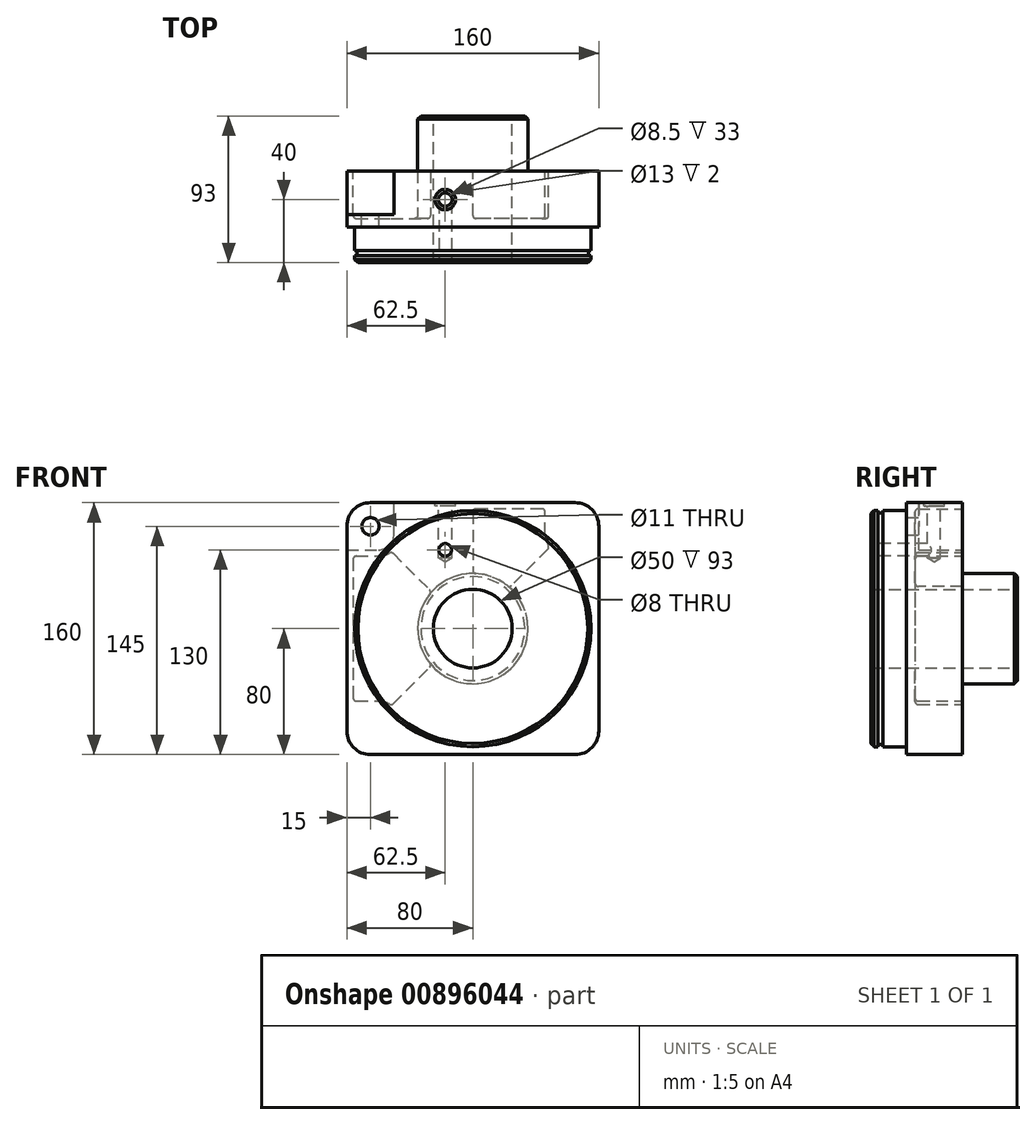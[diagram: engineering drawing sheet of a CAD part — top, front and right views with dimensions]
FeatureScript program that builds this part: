
annotation { "Feature Type Name" : "Feature", "Feature Type Description" : "" }
export const myFeature = defineFeature(function(context is Context, id is Id, definition is map)
    precondition{}
    {
        {
            var Q0;
            Q0=qCreatedBy(makeId("Front.planeOp"),FACE);
            var sketch = newSketch(context, id + "F0", { "sketchPlane" : qUnion([Q0])});
            skLineSegment(sketch, "E0.bottom", {"start": v(65, -80) * mm, "end": v(-65, -80) * mm});
            skLineSegment(sketch, "E0.top", {"start": v(65, 80) * mm, "end": v(-65, 80) * mm});
            skLineSegment(sketch, "E0.left", {"start": v(80, -65) * mm, "end": v(80, 65) * mm});
            skLineSegment(sketch, "E0.right", {"start": v(-80, -65) * mm, "end": v(-80, 65) * mm});
            skPoint(sketch, "E0.middle", {"position": v(0, 0) * mm});
            skPoint(sketch, "E1.visualSharp", {"position": v(-80, 80) * mm});
            skArc(sketch, "E1.filletArc", {"start": v(-65, 80) * mm, "mid": v(-75.6, 75.6) * mm, "end": v(-80, 65) * mm});
            skPoint(sketch, "E2.visualSharp", {"position": v(80, 80) * mm});
            skArc(sketch, "E2.filletArc", {"start": v(80, 65) * mm, "mid": v(75.6, 75.6) * mm, "end": v(65, 80) * mm});
            skPoint(sketch, "E3.visualSharp", {"position": v(80, -80) * mm});
            skArc(sketch, "E3.filletArc", {"start": v(65, -80) * mm, "mid": v(75.6, -75.6) * mm, "end": v(80, -65) * mm});
            skPoint(sketch, "E4.visualSharp", {"position": v(-80, -80) * mm});
            skArc(sketch, "E4.filletArc", {"start": v(-80, -65) * mm, "mid": v(-75.6, -75.6) * mm, "end": v(-65, -80) * mm});
            skLineSegment(sketch, "E5", {"start": v(-80, 50) * mm, "end": v(-60, 50) * mm});
            skLineSegment(sketch, "E6", {"start": v(-50, 60) * mm, "end": v(-50, 80) * mm});
            skPoint(sketch, "E7.visualSharp", {"position": v(-50, 50) * mm});
            skArc(sketch, "E7.filletArc", {"start": v(-60, 50) * mm, "mid": v(-52.93, 52.93) * mm, "end": v(-50, 60) * mm});
            skCircle(sketch, "E8", {"center": v(-65, 65) * mm, "radius": 5.5 * mm});
            skLineSegment(sketch, "E9", {"start": v(0, 0) * mm, "end": v(-65, 65) * mm, "construction": true});
            skLineSegment(sketch, "E10.0", {"start": v(-46, 60) * mm, "end": v(-46, 74) * mm, "construction": true});
            skArc(sketch, "E10.1", {"start": v(-60, 46) * mm, "mid": v(-56.31, 46.5) * mm, "end": v(-52.89, 47.94) * mm});
            skLineSegment(sketch, "E10.2", {"start": v(-74, 46) * mm, "end": v(-60, 46) * mm});
            skCircle(sketch, "E11", {"center": v(0, 0) * mm, "radius": 35 * mm});
            skLineSegment(sketch, "E12", {"start": v(-76, 44) * mm, "end": v(-76, 0) * mm});
            skLineSegment(sketch, "E13", {"start": v(-50.46, 47.63) * mm, "end": v(-26.12, 23.3) * mm});
            skLineSegment(sketch, "E14", {"start": v(-47.63, 50.46) * mm, "end": v(-23.3, 26.12) * mm, "construction": true});
            skLineSegment(sketch, "E15", {"start": v(-44, 76) * mm, "end": v(-2, 76) * mm, "construction": true});
            skLineSegment(sketch, "E16", {"start": v(0, 74) * mm, "end": v(0, 35) * mm});
            skArc(sketch, "E17.trimOffspring", {"start": v(-47.94, 52.89) * mm, "mid": v(-46.5, 56.31) * mm, "end": v(-46, 60) * mm, "construction": true});
            skLineSegment(sketch, "E18.MirrorCS", {"start": v(-76, -44) * mm, "end": v(-76, 0) * mm});
            skLineSegment(sketch, "E19.MirrorCS", {"start": v(-74, -46) * mm, "end": v(-60, -46) * mm});
            skArc(sketch, "E20.MirrorCS", {"start": v(-60, -46) * mm, "mid": v(-56.31, -46.5) * mm, "end": v(-52.89, -47.94) * mm});
            skLineSegment(sketch, "E21.MirrorCS", {"start": v(-50.46, -47.63) * mm, "end": v(-26.12, -23.3) * mm});
            skPoint(sketch, "E22.visualSharp", {"position": v(0, 76) * mm});
            skArc(sketch, "E22.filletArc", {"start": v(0, 74) * mm, "mid": v(-0.59, 75.41) * mm, "end": v(-2, 76) * mm, "construction": true});
            skPoint(sketch, "E23.visualSharp", {"position": v(-46, 76) * mm});
            skArc(sketch, "E23.filletArc", {"start": v(-44, 76) * mm, "mid": v(-45.41, 75.41) * mm, "end": v(-46, 74) * mm, "construction": true});
            skPoint(sketch, "E24.visualSharp", {"position": v(-48.79, 51.62) * mm});
            skArc(sketch, "E24.filletArc", {"start": v(-47.94, 52.89) * mm, "mid": v(-48.2, 51.62) * mm, "end": v(-47.63, 50.46) * mm, "construction": true});
            skPoint(sketch, "E25.visualSharp", {"position": v(-51.62, 48.79) * mm});
            skArc(sketch, "E25.filletArc", {"start": v(-50.46, 47.63) * mm, "mid": v(-51.62, 48.2) * mm, "end": v(-52.89, 47.94) * mm});
            skPoint(sketch, "E26.visualSharp", {"position": v(-76, 46) * mm});
            skArc(sketch, "E26.filletArc", {"start": v(-74, 46) * mm, "mid": v(-75.41, 45.41) * mm, "end": v(-76, 44) * mm});
            skPoint(sketch, "E27.visualSharp", {"position": v(-76, -46) * mm});
            skArc(sketch, "E27.filletArc", {"start": v(-76, -44) * mm, "mid": v(-75.41, -45.41) * mm, "end": v(-74, -46) * mm});
            skPoint(sketch, "E28.visualSharp", {"position": v(-51.62, -48.79) * mm});
            skArc(sketch, "E28.filletArc", {"start": v(-52.89, -47.94) * mm, "mid": v(-51.62, -48.2) * mm, "end": v(-50.46, -47.63) * mm});
            skLineSegment(sketch, "E29.MirrorCS", {"start": v(44, 76) * mm, "end": v(2, 76) * mm});
            skArc(sketch, "E30.MirrorCS", {"start": v(0, 74) * mm, "mid": v(0.59, 75.41) * mm, "end": v(2, 76) * mm});
            skArc(sketch, "E31.MirrorCS", {"start": v(44, 76) * mm, "mid": v(45.41, 75.41) * mm, "end": v(46, 74) * mm});
            skLineSegment(sketch, "E32.MirrorCS", {"start": v(46, 60) * mm, "end": v(46, 74) * mm});
            skArc(sketch, "E33.MirrorCS", {"start": v(47.94, 52.89) * mm, "mid": v(46.5, 56.31) * mm, "end": v(46, 60) * mm});
            skArc(sketch, "E34.MirrorCS", {"start": v(47.94, 52.89) * mm, "mid": v(48.2, 51.62) * mm, "end": v(47.63, 50.46) * mm});
            skLineSegment(sketch, "E35.MirrorCS", {"start": v(47.63, 50.46) * mm, "end": v(23.3, 26.12) * mm});
            skSolve(sketch);
        }
        {
            var Q0;
            Q0 = qSketchRegion(id + "F0", true);
            var Q1;
            Q1=makeQuery(id+"F0.imprint","IMPRINT",FACE,{"disambiguationData":[TD([[makeQuery(id+"F0.imprint","IMPRINT",EDGE,{"derivedFrom":sQuery(id+"F0.wireOp",EDGE,"E10.0")}),-1.0]])]});
            var Q2;
            {var subQ0=sQuery(id+"F0.wireOp",EDGE,"E11");var subQ1=makeQuery(id+"F0.imprint","INTERSECT",VERTEX,{"derivedFrom":[subQ0,sQuery(id+"F0.wireOp",EDGE,"E14")]});Q2=makeQuery(id+"F0.imprint","IMPRINT",FACE,{"disambiguationData":[TD([[makeQuery(id+"F0.imprint","IMPRINT",EDGE,{"disambiguationData":[TD([[subQ1,1.0]])],"derivedFrom":subQ0}),1.0]])]});}
            var Q3;
            Q3=makeQuery(id+"F0.imprint","IMPRINT",FACE,{"disambiguationData":[TD([[makeQuery(id+"F0.imprint","IMPRINT",EDGE,{"derivedFrom":sQuery(id+"F0.wireOp",EDGE,"E10.1")}),-1.0]])]});
            var Q4;
            Q4=makeQuery(id+"F0.imprint","IMPRINT",FACE,{"disambiguationData":[TD([[makeQuery(id+"F0.imprint","IMPRINT",EDGE,{"derivedFrom":sQuery(id+"F0.wireOp",EDGE,"E8")}),1.0]])]});
            var Q5;
            {var subQ0=sQuery(id+"F0.wireOp",EDGE,"E16");Q5=makeQuery(id+"F0.imprint","IMPRINT",FACE,{"disambiguationData":[TD([[makeQuery(id+"F0.imprint","IMPRINT",EDGE,{"derivedFrom":subQ0}),1.0]])]});}
            extrude(context, id + "F1", {"entities" : qUnion([Q0, Q1, Q2, Q3, Q4, Q5]), "depth" : (58 - 22.5) * mm, "offsetDistance" : 25 * mm});
        }
        {
            var Q0;
            {var subQ0=sQuery(id+"F0.wireOp",EDGE,"E11");var subQ1=makeQuery(id+"F0.imprint","INTERSECT",VERTEX,{"derivedFrom":[subQ0,sQuery(id+"F0.wireOp",EDGE,"E14")]});Q0=makeQuery(id+"F0.imprint","IMPRINT",FACE,{"disambiguationData":[TD([[makeQuery(id+"F0.imprint","IMPRINT",EDGE,{"disambiguationData":[TD([[subQ1,1.0]])],"derivedFrom":subQ0}),1.0]])]});}
            extrude(context, id + "F2", {"entities" : qUnion([Q0]), "operationType" : NewBodyOperationType.ADD, "oppositeDirection" : true, "depth" : (93 - 58) * mm, "offsetDistance" : 25 * mm});
        }
        {
            var Q0;
            Q0=makeQuery(id+"F0.imprint","IMPRINT",FACE,{"disambiguationData":[TD([[makeQuery(id+"F0.imprint","IMPRINT",EDGE,{"derivedFrom":sQuery(id+"F0.wireOp",EDGE,"E8")}),1.0]])]});
            var Q1;
            Q1=makeQuery(id+"F1.opExtrude","CAP_FACE",FACE,{"disambiguationData":[OSD([sQuery(id+"F0.wireOp",EDGE,"E0.bottom"),sQuery(id+"F0.wireOp",EDGE,"E0.top"),sQuery(id+"F0.wireOp",EDGE,"E0.left"),sQuery(id+"F0.wireOp",EDGE,"E0.right"),sQuery(id+"F0.wireOp",EDGE,"E1.filletArc"),sQuery(id+"F0.wireOp",EDGE,"E2.filletArc"),sQuery(id+"F0.wireOp",EDGE,"E3.filletArc"),sQuery(id+"F0.wireOp",EDGE,"E4.filletArc")])],"isStart":false});
            extrude(context, id + "F3", {"entities" : qUnion([Q0]), "operationType" : NewBodyOperationType.REMOVE, "endBound" : BoundingType.UP_TO_SURFACE, "depth" : 25 * mm, "endBoundEntityFace" : qUnion([Q1]), "offsetDistance" : 25 * mm});
        }
        {
            var Q0;
            {var subQ0=sQuery(id+"F0.wireOp",EDGE,"E1.filletArc");Q0=makeQuery(id+"F0.imprint","IMPRINT",FACE,{"disambiguationData":[TD([[makeQuery(id+"F0.imprint","IMPRINT",EDGE,{"derivedFrom":subQ0}),1.0]])]});}
            extrude(context, id + "F4", {"entities" : qUnion([Q0]), "operationType" : NewBodyOperationType.REMOVE, "depth" : (35.5 - 8) * mm, "offsetDistance" : 25 * mm});
        }
        {
            var Q0;
            {var subQ0=sQuery(id+"F0.wireOp",EDGE,"E16");Q0=makeQuery(id+"F0.imprint","IMPRINT",FACE,{"disambiguationData":[TD([[makeQuery(id+"F0.imprint","IMPRINT",EDGE,{"derivedFrom":subQ0}),1.0]])]});}
            extrude(context, id + "F5", {"entities" : qUnion([Q0]), "operationType" : NewBodyOperationType.REMOVE, "depth" : 30 * mm, "offsetDistance" : 25 * mm});
        }
        {
            var Q0;
            Q0=makeQuery(id+"F0.imprint","IMPRINT",FACE,{"disambiguationData":[TD([[makeQuery(id+"F0.imprint","IMPRINT",EDGE,{"derivedFrom":sQuery(id+"F0.wireOp",EDGE,"E10.1")}),-1.0]])]});
            extrude(context, id + "F6", {"entities" : qUnion([Q0]), "operationType" : NewBodyOperationType.REMOVE, "depth" : 30 * mm, "offsetDistance" : 25 * mm});
        }
        {
            var Q0;
            Q0=makeQuery(id+"F5.boolean.opBoolean","COPY",EDGE,{"derivedFrom":makeQuery(id+"F5.opExtrude","SWEPT_EDGE",EDGE,{"disambiguationData":[OSD([sQuery(id+"F0.wireOp",EDGE,"E11"),sQuery(id+"F0.wireOp",EDGE,"E16")])]})});
            var Q1;
            Q1=makeQuery(id+"F5.boolean.opBoolean","COPY",EDGE,{"derivedFrom":makeQuery(id+"F5.opExtrude","SWEPT_EDGE",EDGE,{"disambiguationData":[OSD([sQuery(id+"F0.wireOp",EDGE,"E11"),sQuery(id+"F0.wireOp",EDGE,"E14")])]})});
            var Q2;
            Q2=makeQuery(id+"FySSFkN4dkQmMlL_1.2.F6.boolean.opBoolean","COPY",EDGE,{"derivedFrom":makeQuery(id+"FySSFkN4dkQmMlL_1.2.F6.opExtrude","SWEPT_EDGE",EDGE,{"disambiguationData":[OSD([sQuery(id+"F0.wireOp",EDGE,"E11"),sQuery(id+"F0.wireOp",EDGE,"E21.MirrorCS")])]})});
            var Q3;
            Q3=makeQuery(id+"FySSFkN4dkQmMlL_1.2.F6.boolean.opBoolean","COPY",EDGE,{"derivedFrom":makeQuery(id+"FySSFkN4dkQmMlL_1.2.F6.opExtrude","SWEPT_EDGE",EDGE,{"disambiguationData":[OSD([sQuery(id+"F0.wireOp",EDGE,"E11"),sQuery(id+"F0.wireOp",EDGE,"E13")])]})});
            var Q4;
            Q4=makeQuery(id+"FySSFkN4dkQmMlL_1.1.F6.boolean.opBoolean","COPY",EDGE,{"derivedFrom":makeQuery(id+"FySSFkN4dkQmMlL_1.1.F6.opExtrude","SWEPT_EDGE",EDGE,{"disambiguationData":[OSD([sQuery(id+"F0.wireOp",EDGE,"E11"),sQuery(id+"F0.wireOp",EDGE,"E21.MirrorCS")])]})});
            var Q5;
            Q5=makeQuery(id+"FySSFkN4dkQmMlL_1.1.F6.boolean.opBoolean","COPY",EDGE,{"derivedFrom":makeQuery(id+"FySSFkN4dkQmMlL_1.1.F6.opExtrude","SWEPT_EDGE",EDGE,{"disambiguationData":[OSD([sQuery(id+"F0.wireOp",EDGE,"E11"),sQuery(id+"F0.wireOp",EDGE,"E13")])]})});
            var Q6;
            Q6=makeQuery(id+"F6.boolean.opBoolean","COPY",EDGE,{"derivedFrom":makeQuery(id+"F6.opExtrude","SWEPT_EDGE",EDGE,{"disambiguationData":[OSD([sQuery(id+"F0.wireOp",EDGE,"E11"),sQuery(id+"F0.wireOp",EDGE,"E13")])]})});
            var Q7;
            Q7=makeQuery(id+"F6.boolean.opBoolean","COPY",EDGE,{"derivedFrom":makeQuery(id+"F6.opExtrude","SWEPT_EDGE",EDGE,{"disambiguationData":[OSD([sQuery(id+"F0.wireOp",EDGE,"E11"),sQuery(id+"F0.wireOp",EDGE,"E21.MirrorCS")])]})});
            fillet(context, id + "F7", {"entities" : qUnion([Q0, Q1, Q2, Q3, Q4, Q5, Q6, Q7]), "radius" : 2 * mm, "tangentPropagation" : true, "allowEdgeOverflow" : false});
        }
        {
            var Q0;
            Q0=makeQuery(id+"FySSFkN4dkQmMlL_1.2.F6.boolean.opBoolean","COPY",FACE,{"derivedFrom":makeQuery(id+"FySSFkN4dkQmMlL_1.2.F6.opExtrude","CAP_FACE",FACE,{"disambiguationData":[OSD([sQuery(id+"F0.wireOp",EDGE,"E10.1"),sQuery(id+"F0.wireOp",EDGE,"E10.2"),sQuery(id+"F0.wireOp",EDGE,"E11"),sQuery(id+"F0.wireOp",EDGE,"E12"),sQuery(id+"F0.wireOp",EDGE,"E13"),sQuery(id+"F0.wireOp",EDGE,"E18.MirrorCS"),sQuery(id+"F0.wireOp",EDGE,"E19.MirrorCS"),sQuery(id+"F0.wireOp",EDGE,"E20.MirrorCS"),sQuery(id+"F0.wireOp",EDGE,"E21.MirrorCS"),sQuery(id+"F0.wireOp",EDGE,"E25.filletArc"),sQuery(id+"F0.wireOp",EDGE,"E26.filletArc"),sQuery(id+"F0.wireOp",EDGE,"E27.filletArc"),sQuery(id+"F0.wireOp",EDGE,"E28.filletArc")])],"isStart":false})});
            var Q1;
            Q1=makeQuery(id+"FySSFkN4dkQmMlL_1.1.F6.boolean.opBoolean","COPY",FACE,{"derivedFrom":makeQuery(id+"FySSFkN4dkQmMlL_1.1.F6.opExtrude","CAP_FACE",FACE,{"disambiguationData":[OSD([sQuery(id+"F0.wireOp",EDGE,"E10.1"),sQuery(id+"F0.wireOp",EDGE,"E10.2"),sQuery(id+"F0.wireOp",EDGE,"E11"),sQuery(id+"F0.wireOp",EDGE,"E12"),sQuery(id+"F0.wireOp",EDGE,"E13"),sQuery(id+"F0.wireOp",EDGE,"E18.MirrorCS"),sQuery(id+"F0.wireOp",EDGE,"E19.MirrorCS"),sQuery(id+"F0.wireOp",EDGE,"E20.MirrorCS"),sQuery(id+"F0.wireOp",EDGE,"E21.MirrorCS"),sQuery(id+"F0.wireOp",EDGE,"E25.filletArc"),sQuery(id+"F0.wireOp",EDGE,"E26.filletArc"),sQuery(id+"F0.wireOp",EDGE,"E27.filletArc"),sQuery(id+"F0.wireOp",EDGE,"E28.filletArc")])],"isStart":false})});
            var Q2;
            Q2=makeQuery(id+"F5.boolean.opBoolean","COPY",FACE,{"derivedFrom":makeQuery(id+"F5.opExtrude","CAP_FACE",FACE,{"disambiguationData":[OSD([sQuery(id+"F0.wireOp",EDGE,"E10.0"),sQuery(id+"F0.wireOp",EDGE,"E11"),sQuery(id+"F0.wireOp",EDGE,"E14"),sQuery(id+"F0.wireOp",EDGE,"E15"),sQuery(id+"F0.wireOp",EDGE,"E16"),sQuery(id+"F0.wireOp",EDGE,"E17.trimOffspring"),sQuery(id+"F0.wireOp",EDGE,"E22.filletArc"),sQuery(id+"F0.wireOp",EDGE,"E23.filletArc"),sQuery(id+"F0.wireOp",EDGE,"E24.filletArc")])],"isStart":false})});
            var Q3;
            Q3=makeQuery(id+"F6.boolean.opBoolean","COPY",FACE,{"derivedFrom":makeQuery(id+"F6.opExtrude","CAP_FACE",FACE,{"disambiguationData":[OSD([sQuery(id+"F0.wireOp",EDGE,"E10.1"),sQuery(id+"F0.wireOp",EDGE,"E10.2"),sQuery(id+"F0.wireOp",EDGE,"E11"),sQuery(id+"F0.wireOp",EDGE,"E12"),sQuery(id+"F0.wireOp",EDGE,"E13"),sQuery(id+"F0.wireOp",EDGE,"E18.MirrorCS"),sQuery(id+"F0.wireOp",EDGE,"E19.MirrorCS"),sQuery(id+"F0.wireOp",EDGE,"E20.MirrorCS"),sQuery(id+"F0.wireOp",EDGE,"E21.MirrorCS"),sQuery(id+"F0.wireOp",EDGE,"E25.filletArc"),sQuery(id+"F0.wireOp",EDGE,"E26.filletArc"),sQuery(id+"F0.wireOp",EDGE,"E27.filletArc"),sQuery(id+"F0.wireOp",EDGE,"E28.filletArc")])],"isStart":false})});
            fillet(context, id + "F8", {"entities" : qUnion([Q0, Q1, Q2, Q3]), "radius" : 2 * mm, "tangentPropagation" : true, "allowEdgeOverflow" : false});
        }
        {
            var Q0;
            Q0=makeQuery(id+"F1.opExtrude","CAP_FACE",FACE,{"disambiguationData":[OSD([sQuery(id+"F0.wireOp",EDGE,"E0.bottom"),sQuery(id+"F0.wireOp",EDGE,"E0.top"),sQuery(id+"F0.wireOp",EDGE,"E0.left"),sQuery(id+"F0.wireOp",EDGE,"E0.right"),sQuery(id+"F0.wireOp",EDGE,"E1.filletArc"),sQuery(id+"F0.wireOp",EDGE,"E2.filletArc"),sQuery(id+"F0.wireOp",EDGE,"E3.filletArc"),sQuery(id+"F0.wireOp",EDGE,"E4.filletArc")])],"isStart":false});
            var sketch = newSketch(context, id + "F9", { "sketchPlane" : qUnion([Q0])});
            skCircle(sketch, "E36", {"center": v(0, 0) * mm, "radius": 75 * mm});
            skSolve(sketch);
        }
        {
            var Q0;
            Q0=makeQuery(id+"F9.imprint","IMPRINT",FACE,{"disambiguationData":[TD([[makeQuery(id+"F9.imprint","IMPRINT",EDGE,{"derivedFrom":sQuery(id+"F9.wireOp",EDGE,"E36")}),1.0]])]});
            extrude(context, id + "F10", {"entities" : qUnion([Q0]), "operationType" : NewBodyOperationType.ADD, "depth" : 22.5 * mm, "offsetDistance" : 25 * mm});
        }
        {
            var Q0;
            Q0=makeQuery(id+"F2.opExtrude","CAP_FACE",FACE,{"disambiguationData":[OSD([sQuery(id+"F0.wireOp",EDGE,"E11")])],"isStart":false});
            var sketch = newSketch(context, id + "F11", { "sketchPlane" : qUnion([Q0])});
            skPoint(sketch, "E37", {"position": v(0, 0) * mm});
            skSolve(sketch);
        }
        {
            var Q0;
            Q0=sQuery(id+"F11.wireOp",VERTEX,"E37");
            var Q1;
            Q1=makeQuery(id+"F1.opExtrude","SWEPT_BODY",BODY,{"disambiguationData":[OSD([sQuery(id+"F0.wireOp",EDGE,"E0.bottom"),sQuery(id+"F0.wireOp",EDGE,"E0.top"),sQuery(id+"F0.wireOp",EDGE,"E0.left"),sQuery(id+"F0.wireOp",EDGE,"E0.right"),sQuery(id+"F0.wireOp",EDGE,"E1.filletArc"),sQuery(id+"F0.wireOp",EDGE,"E2.filletArc"),sQuery(id+"F0.wireOp",EDGE,"E3.filletArc"),sQuery(id+"F0.wireOp",EDGE,"E4.filletArc")])]});
            hole(context, id + "F12", {"style" : HoleStyle.SIMPLE, "endStyle" : HoleEndStyle.THROUGH, "holeDiameter" : 50 * mm, "majorDiameter" : 5 * mm, "isTappedThrough" : true, "tappedDepth" : 20 * mm, "tapClearance" : 3, "startFromSketch" : true, "locations" : qUnion([Q0]), "scope" : qUnion([Q1])});
        }
        {
            var Q0;
            Q0=makeQuery(id+"F1.opExtrude","SWEPT_FACE",FACE,{"disambiguationData":[OSD([sQuery(id+"F0.wireOp",EDGE,"E0.top")])]});
            var sketch = newSketch(context, id + "F13", { "sketchPlane" : qUnion([Q0])});
            skPoint(sketch, "E38", {"position": v(-17.5, -18) * mm});
            skSolve(sketch);
        }
        {
            var Q0;
            Q0=sQuery(id+"F13.wireOp",VERTEX,"E38");
            var Q1;
            Q1=makeQuery(id+"F1.opExtrude","SWEPT_BODY",BODY,{"disambiguationData":[OSD([sQuery(id+"F0.wireOp",EDGE,"E0.bottom"),sQuery(id+"F0.wireOp",EDGE,"E0.top"),sQuery(id+"F0.wireOp",EDGE,"E0.left"),sQuery(id+"F0.wireOp",EDGE,"E0.right"),sQuery(id+"F0.wireOp",EDGE,"E1.filletArc"),sQuery(id+"F0.wireOp",EDGE,"E2.filletArc"),sQuery(id+"F0.wireOp",EDGE,"E3.filletArc"),sQuery(id+"F0.wireOp",EDGE,"E4.filletArc")])]});
            hole(context, id + "F14", {"style" : HoleStyle.C_BORE, "endStyle" : HoleEndStyle.BLIND, "holeDiameter" : 8.5 * mm, "cBoreDiameter" : 13 * mm, "cBoreDepth" : 2 * mm, "majorDiameter" : 10 * mm, "holeDepth" : 35 * mm, "isTappedThrough" : true, "tappedDepth" : 20 * mm, "tapClearance" : 3, "startFromSketch" : true, "locations" : qUnion([Q0]), "scope" : qUnion([Q1])});
        }
        {
            var Q0;
            Q0=qCreatedBy(makeId("Right.planeOp"),FACE);
            var sketch = newSketch(context, id + "F15", { "sketchPlane" : qUnion([Q0])});
            skLineSegment(sketch, "E39.bottom", {"start": v(-53.5, 75) * mm, "end": v(-50.5, 75) * mm});
            skLineSegment(sketch, "E39.top", {"start": v(-53.5, 73.5) * mm, "end": v(-50.5, 73.5) * mm});
            skLineSegment(sketch, "E39.left", {"start": v(-53.5, 75) * mm, "end": v(-53.5, 73.5) * mm});
            skLineSegment(sketch, "E39.right", {"start": v(-50.5, 75) * mm, "end": v(-50.5, 73.5) * mm});
            skLineSegment(sketch, "E40", {"start": v(0, 0) * mm, "end": v(-58, 0) * mm, "construction": true});
            skSolve(sketch);
        }
        {
            var Q0;
            Q0 = qSketchRegion(id + "F15", true);
            var Q1;
            Q1=sQuery(id+"F15.wireOp",EDGE,"E40");
            revolve(context, id + "F16", {"operationType" : NewBodyOperationType.REMOVE, "surfaceOperationType" : NewSurfaceOperationType.NEW, "entities" : qUnion([Q0]), "axis" : qUnion([Q1]), "revolveType" : RevolveType.FULL, "oppositeDirection" : true});
        }
        {
            var Q0;
            Q0=makeQuery(id+"F10.opExtrude","CAP_EDGE",EDGE,{"disambiguationData":[OSD([sQuery(id+"F9.wireOp",EDGE,"E36")])],"isStart":false});
            var Q1;
            Q1=makeQuery(id+"F2.opExtrude","CAP_EDGE",EDGE,{"disambiguationData":[OSD([sQuery(id+"F0.wireOp",EDGE,"E11")])],"isStart":false});
            chamfer(context, id + "F17", {"entities" : qUnion([Q0, Q1]), "width" : 2 * mm, "tangentPropagation" : true});
        }
        {
            var Q0;
            Q0=makeQuery(id+"F10.opExtrude","CAP_FACE",FACE,{"disambiguationData":[OSD([sQuery(id+"F9.wireOp",EDGE,"E36")])],"isStart":false});
            var sketch = newSketch(context, id + "F18", { "sketchPlane" : qUnion([Q0])});
            skPoint(sketch, "E41.0", {"position": v(-17.5, 80) * mm});
            skLineSegment(sketch, "E42", {"start": v(-17.5, 80) * mm, "end": v(-17.5, 50) * mm, "construction": true});
            skSolve(sketch);
        }
        {
            var Q0;
            Q0=sQuery(id+"F18.wireOp",VERTEX,"E42.end");
            var Q1;
            Q1=makeQuery(id+"F1.opExtrude","SWEPT_BODY",BODY,{"disambiguationData":[OSD([sQuery(id+"F0.wireOp",EDGE,"E0.bottom"),sQuery(id+"F0.wireOp",EDGE,"E0.top"),sQuery(id+"F0.wireOp",EDGE,"E0.left"),sQuery(id+"F0.wireOp",EDGE,"E0.right"),sQuery(id+"F0.wireOp",EDGE,"E1.filletArc"),sQuery(id+"F0.wireOp",EDGE,"E2.filletArc"),sQuery(id+"F0.wireOp",EDGE,"E3.filletArc"),sQuery(id+"F0.wireOp",EDGE,"E4.filletArc")])]});
            hole(context, id + "F19", {"style" : HoleStyle.SIMPLE, "endStyle" : HoleEndStyle.BLIND, "holeDiameter" : 8 * mm, "majorDiameter" : 5 * mm, "holeDepth" : 40 * mm, "isTappedThrough" : true, "tappedDepth" : 20 * mm, "tapClearance" : 3, "startFromSketch" : true, "locations" : qUnion([Q0]), "scope" : qUnion([Q1])});
        }
    });
